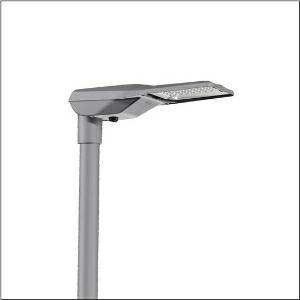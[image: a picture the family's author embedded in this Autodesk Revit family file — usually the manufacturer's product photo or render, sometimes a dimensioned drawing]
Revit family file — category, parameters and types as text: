
# Revit family: streetlight_sl_21_iq_mini___p0_5a_5xe2v31u08hb_fe50
name_source: partatom
category: Lighting Fixtures
units: mm (PartAtom-declared; Revit-internal decimal feet)

## family parameters
Cut with Voids When Loaded = No
Host = Face
Light Source = No
Part Type = Normal
Room Calculation Point = No
Round Connector Dimension = Use Diameter
Shared = No

## types (1)
- --- (1 x LED, 9580 lm, 71 W, 3000K)
    Apparent Load = 71 VA
    CIE Flux Codes = 37 73 96 100 100
    Color Rendering = 70
    Color Temperature = 3000K
    Default Elevation = 1800 mm
    Description = Streetlight SL 21 iQ mini, mast luminaire, primary light control with lens, of PMMA, primary optical cover: cover, of toughened safety glass, transparent, light distribution: P0.5a, light emission: direct distribution, primary light characteristic: asymmetric, installation type: post-top, side-entry, LED, High Power LED, rated luminous flux: 9.580lm, luminous efficacy: 135lm/W, light colour: 730, colour temperature: 3000K, control gear: iQ-Street Remote, D4i with power reduction, control: pre-setting: logarithmic dimming characteristic, Street-Remote, Auto-Match, Temp-Guard, Lumen-Switch, Night-Set, Smart-Wire, Light-Fading, Desk-Remote (wireless, voltage-free reading and setting of iQ features in the workshop via application-optimized NFC function/RFID function), optimised constant luminous flux control (CLO 2.0), mains connection: 220..240V, AC, 50/60Hz, start of lifetime: 71W, end of service life: 75W, reduction: 30W, luminaire housing, of diecast aluminium, powder-coated, SITECO metallic grey (DB 702S), corrosivity category C5 high according to DIN EN ISO 12944, please order mast flange separately, inclination adjustable: 0°, 5°, 10°, 15°, sealing non-destructively replaceable, multi-level sealing system, length: 628mm, width: 235mm, height: 110mm, mast flange for spigot size: 42mm (side-entry): 5XC10008XM4, 60/48mm (side-entry/post-top): 5XC10108XM2, 76/60mm (side-entry/post-top): 5XC10108XM1, mounting height: 4..8m, Smart Interface below, protection rating (complete): IP66, insulation class (complete): insulation class II (safety insulation), certification: CE, ENEC, ENEC+, VDE, impact resistance: IK10, permissible operating ambient temperature for outdoor applications: -40..+50°C, standard-compliant lighting for roads and squares, packaging unit: 1 piece

Light Distribution: P0.5a
    Height = 110 mm
    Lamp = 1 x LED
    Lamp Light Flux = 9580 lm
    Lamp Power = 71 W
    Lamp count = 1
    Length = 625 mm
    Luminous efficacy = 135 lm/W
    Manufacturer = Siteco
    ModVariant = No
    Model = 5XE2V31U08HB
    Number of Poles = 1
    OnlyDefault = Yes
    Power Factor = 1
    Product Name = Streetlight SL 21 iQ mini | P0.5a
    Product group = mast luminaire | pylon top
    ProductGroupID = 6100
    Protection Class = Protection class II
    Protection Degree = IP 66
    RLX_Detail_Level = 1
    RLX_Emergency_Light_Flux = 0 lm
    RLX_Emergency_Type = 0
    RLX_Emergency_Type_DB = No
    RlxData = <blob elided: 93357 chars, md5=3022160c>
    Socket = socket
    Standby Power = 0 W
    System Light Flux = 9580 lm
    System Power = 71 W
    Type Comments = factory setting: luminous flux: 100 % | dim-lin: 254 | 716 mA
    Type Image = l_1003516.jpg
    URL = http://relux.com
    VarID = @adj_078453
    Voltage = 0 V
    Weight = 0.00 kg
    Width = 234 mm

## geometry (parser evidence)
native form markers: Blend x4, Sweep x11
no freeform markers — native parametric forms only
